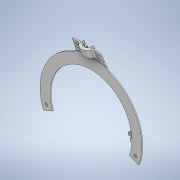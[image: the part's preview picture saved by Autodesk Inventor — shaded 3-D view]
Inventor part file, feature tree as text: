
AUTODESK INVENTOR PART (.ipt)
format: ipt  version: 2020 (Build 240168000, 168)  size: 764,928 bytes
history: native  units: mm
features: reference x94, extrude x15, sketch x14, plane x13, other x9, fillet x5, projected_geometry x3, loft x2
ambient origin geometry x8: Origin, YZ Plane, XZ Plane, XY Plane, X Axis, Y Axis, Z Axis, Center Point
bodies: Solid1 (feature_tree)
feature tree (155):
  extrude  "Extrusion1"  Depth=10.0mm TaperAngle=0.0deg
  plane  "Work Plane2"
  extrude  "Extrusion4"  Depth=10.0mm TaperAngle=0.0deg
  plane  "Work Plane3"
  extrude  "Extrusion5"  Depth=2.0mm TaperAngle=0.0deg
  sketch  "Sketch9"  dims[d18=10.0mm d19=0.0mm d25=2.0mm d26=0.0mm]
  plane  "Work Plane4"
  extrude  "Extrusion6"  [1 undecoded]
  extrude  "Extrusion7"  TaperAngle=0.0deg  [1 undecoded]
  plane  "Work Plane7"
  extrude  "Extrusion10"  Depth=2.0mm TaperAngle=0.0deg
  plane  "Work Plane8"
  plane  "Work Plane9"
  plane  "Work Plane10"
  plane  "Work Plane11"
  plane  "Work Plane12"
  sketch  "Sketch22"  dims[d42=2.8mm d46=0.0mm d47=90.0deg]
  loft  "Loft1"
  loft  "Loft2"
  fillet  "Fillet5"  [1 undecoded]
  other  "Work Axis2"
  plane  "Work Plane13"
  extrude  "Extrusion16"  Depth=2.8mm
  extrude  "Extrusion17"  Depth=4.0mm
  extrude  "Extrusion18"  Depth=8.5mm TaperAngle=0.0deg
  fillet  "Fillet7"  Radius=1.53mm
  plane  "Work Plane14"
  extrude  "Extrusion19"  Depth=0.2mm
  extrude  "Extrusion20"  Depth=0.6mm
  plane  "Work Plane15"
  extrude  "Extrusion21"  Depth=0.512mm TaperAngle=0.0deg
  sketch  "Sketch31"  dims[d78=0.036mm d79=0.0mm d80=0.6mm]
  plane  "Work Plane16"
  extrude  "Extrusion22"  Depth=0.6mm
  fillet  "Fillet8"  Radius=0.5mm
  extrude  "Extrusion23"  [1 undecoded]
  fillet  "Fillet9"  [1 undecoded]
  extrude  "Extrusion24"  [1 undecoded]
  fillet  "Fillet10"  [1 undecoded]
  sketch  "Sketch5"  dims[d0=1.0mm d1=0.0mm d12=10.0mm d13=0.0mm]
  reference  "Reference15"
  reference  "Reference16"
  reference  "Reference17"
  reference  "Reference18"
  reference  "Reference19"
  reference  "Reference20"
  reference  "Reference21"
  reference  "Reference22"
  reference  "Reference23"
  reference  "Reference24"
  reference  "Reference25"
  sketch  "Sketch8"  dims[d14=0.0mm d15=0.0mm d16=10.0mm d17=0.0mm]
  reference  "Reference48"
  reference  "Reference49"
  reference  "Reference50"
  reference  "Reference51"
  reference  "Reference52"
  reference  "Reference53"
  reference  "Reference54"
  reference  "Reference55"
  reference  "Reference56"
  reference  "Reference57"
  reference  "Reference58"
  reference  "Reference59"
  reference  "Reference60"
  reference  "Reference61"
  reference  "Reference62"
  reference  "Reference63"
  sketch  "Sketch10"  dims[d34=-0.5mm d41=-0.5mm]
  reference  "Reference64"
  reference  "Reference65"
  reference  "Reference66"
  reference  "Reference67"
  reference  "Reference68"
  reference  "Reference69"
  reference  "Reference70"
  reference  "Reference77"
  reference  "Reference78"
  other  "Work Axis1"
  reference  "Reference93"
  reference  "Reference94"
  reference  "Reference95"
  reference  "Reference98"
  reference  "Reference99"
  sketch  "Sketch24"  dims[d48=0.0mm d49=90.0deg d52=0.0mm d53=90.0deg d54=2.0mm]
  reference  "Reference101"
  reference  "Reference102"
  sketch  "Sketch25"  dims[d55=3.5mm d56=0.0mm d58=105.0deg]
  reference  "Reference103"
  reference  "Reference104"
  reference  "Reference105"
  reference  "Reference106"
  reference  "Reference107"
  reference  "Reference108"
  reference  "Reference109"
  reference  "Reference110"
  reference  "Reference111"
  reference  "Reference112"
  reference  "Reference113"
  reference  "Reference114"
  reference  "Reference115"
  reference  "Reference116"
  reference  "Reference117"
  reference  "Reference118"
  reference  "Reference119"
  reference  "Reference120"
  reference  "Reference121"
  reference  "Reference122"
  reference  "Reference123"
  reference  "Reference124"
  reference  "Reference125"
  reference  "Reference126"
  reference  "Reference127"
  reference  "Reference128"
  reference  "Reference129"
  reference  "Reference130"
  reference  "Reference131"
  reference  "Reference132"
  reference  "Reference133"
  reference  "Reference134"
  reference  "Reference135"
  reference  "Reference136"
  reference  "Reference137"
  reference  "Reference138"
  reference  "Reference139"
  other  "Edges2"
  sketch  "Sketch26"  dims[d59=105.0deg d60=0.0mm d61=90.0deg d62=0.0mm d63=0.0mm]
  reference  "Reference142"
  reference  "Reference143"
  sketch  "Sketch27"  dims[d64=2.8mm d65=2.8mm]
  sketch  "Sketch28"  dims[d66=0.5mm d67=0.0mm d68=4.0mm]
  reference  "Reference144"
  reference  "Reference147"
  reference  "Reference148"
  sketch  "Sketch29"  dims[d69=0.5mm d70=0.0mm d71=8.5mm d72=0.0mm d73=1.53mm d74=0.0mm]
  projected_geometry  "Projected Loop2"
  reference  "Reference149"
  reference  "Reference150"
  reference  "Reference151"
  reference  "Reference152"
  reference  "Reference153"
  reference  "Reference154"
  sketch  "Sketch30"  dims[d75=8.5mm d76=0.0mm d77=0.2mm]
  reference  "Reference155"
  projected_geometry  "Projected Loop3"
  reference  "Reference156"
  reference  "Reference157"
  projected_geometry  "Projected Loop4"
  sketch  "Sketch32"  dims[d81=1.6mm d82=0.512mm d83=0.0mm d84=0.6mm d57=0.5mm]
  other  "<userpath>\Desktop\Model Stuff\Siberia 840\Ear Piece Holder.iam"
  other  "Ear Piece Holder.iam"
  other  "Ear Piece Holder:1"
  other  "Stick:1"
  other  "<userpath>\Desktop\Model Stuff\Siberia 840\Assembly1.iam"
  other  "Assembly1.iam"
note: 7 required parameter values undecoded (feature->parameter linkage not recoverable at this tier; creation-order binding heuristic only, values carry confidence <= 0.55)
